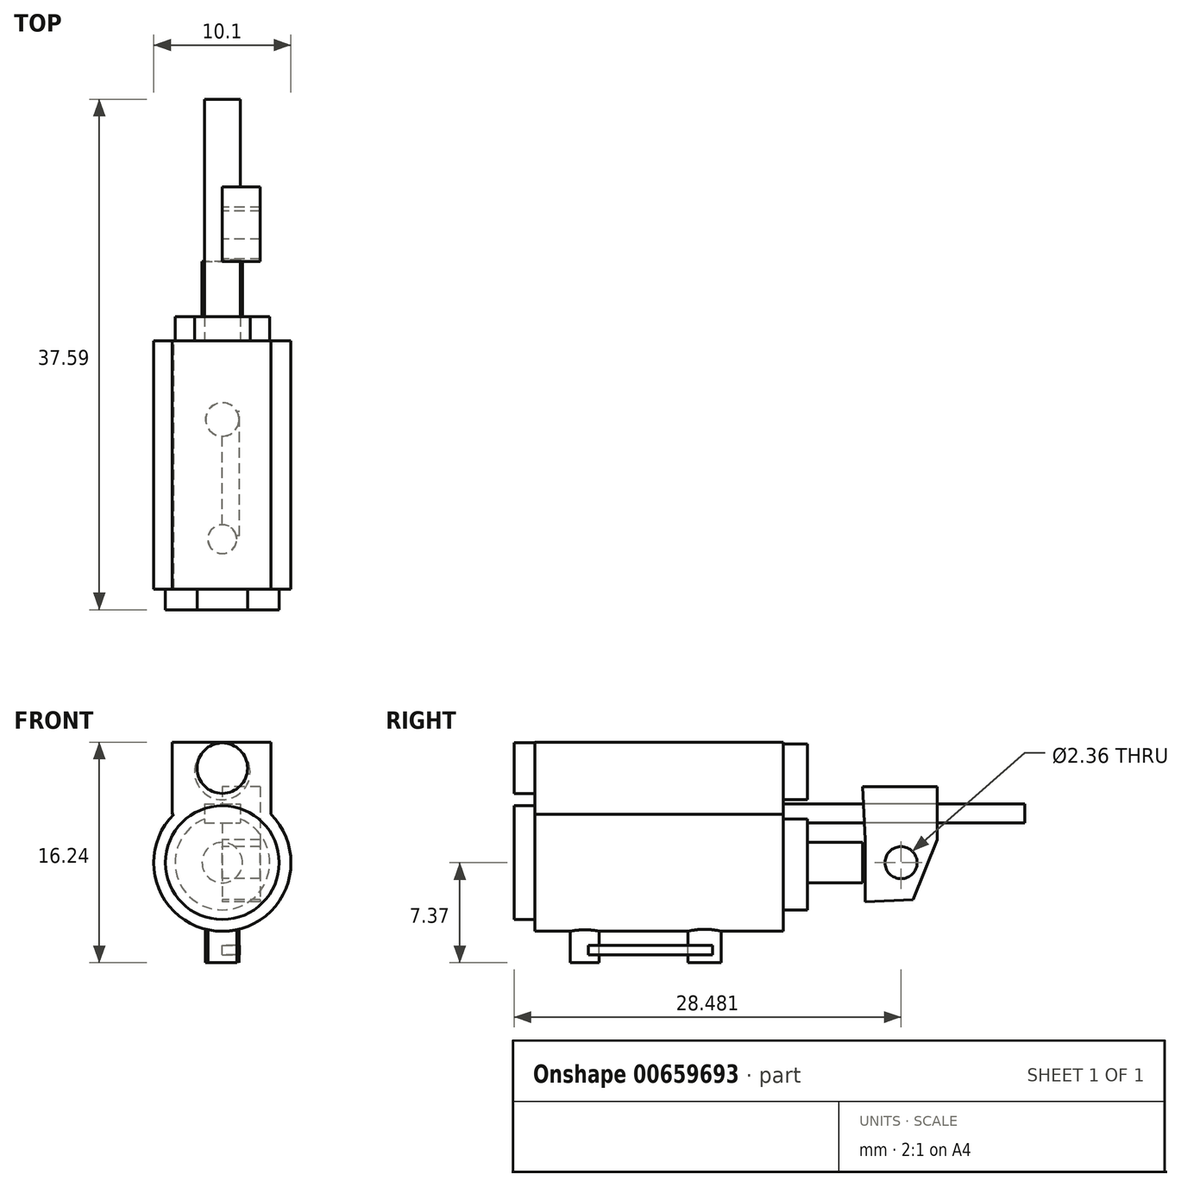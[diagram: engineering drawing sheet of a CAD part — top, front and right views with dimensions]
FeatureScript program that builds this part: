
annotation { "Feature Type Name" : "Feature", "Feature Type Description" : "" }
export const myFeature = defineFeature(function(context is Context, id is Id, definition is map)
    precondition{}
    {
        {
            var Q0;
            Q0=qCreatedBy(makeId("Front.planeOp"),FACE);
            var sketch = newSketch(context, id + "F0", { "sketchPlane" : qUnion([Q0])});
            skCircle(sketch, "E0", {"center": v(0, 0) * mm, "radius": 5.05 * mm});
            skLineSegment(sketch, "E1.bottom", {"start": v(-3.69, 8.87) * mm, "end": v(3.58, 8.87) * mm});
            skLineSegment(sketch, "E1.top", {"start": v(-3.69, 3.57) * mm, "end": v(3.58, 3.57) * mm});
            skLineSegment(sketch, "E1.left", {"start": v(-3.69, 8.87) * mm, "end": v(-3.69, 3.57) * mm});
            skLineSegment(sketch, "E1.right", {"start": v(3.58, 8.87) * mm, "end": v(3.58, 3.57) * mm});
            skSolve(sketch);
        }
        {
            var Q0;
            Q0 = qSketchRegion(id + "F0", true);
            extrude(context, id + "F1", {"entities" : qUnion([Q0]), "depth" : 18.29 * mm, "offsetDistance" : 25.4 * mm});
        }
        {
            var Q0;
            Q0=qCreatedBy(makeId("Front.planeOp"),FACE);
            var sketch = newSketch(context, id + "F2", { "sketchPlane" : qUnion([Q0])});
            skCircle(sketch, "E2", {"center": v(0, 0) * mm, "radius": 3.48 * mm});
            skCircle(sketch, "E3", {"center": v(0, 6.69) * mm, "radius": 2.05 * mm});
            skSolve(sketch);
        }
        {
            var Q0;
            Q0 = qSketchRegion(id + "F2", true);
            extrude(context, id + "F3", {"entities" : qUnion([Q0]), "operationType" : NewBodyOperationType.ADD, "oppositeDirection" : true, "depth" : 1.78 * mm, "offsetDistance" : 25.4 * mm});
        }
        {
            var Q0;
            Q0=qCreatedBy(makeId("Front.planeOp"),FACE);
            var sketch = newSketch(context, id + "F4", { "sketchPlane" : qUnion([Q0])});
            skCircle(sketch, "E4", {"center": v(0, 0) * mm, "radius": 4.19 * mm});
            skCircle(sketch, "E5", {"center": v(0, 6.96) * mm, "radius": 1.86 * mm});
            skSolve(sketch);
        }
        {
            var Q0;
            Q0 = qSketchRegion(id + "F4", true);
            extrude(context, id + "F5", {"entities" : qUnion([Q0]), "operationType" : NewBodyOperationType.ADD, "depth" : 19.8 * mm, "offsetDistance" : 25.4 * mm});
        }
        {
            var Q0;
            Q0=qCreatedBy(makeId("Top.planeOp"),FACE);
            var sketch = newSketch(context, id + "F6", { "sketchPlane" : qUnion([Q0])});
            skCircle(sketch, "E6", {"center": v(0, -14.6) * mm, "radius": 1.06 * mm});
            skCircle(sketch, "E7", {"center": v(0, -5.8) * mm, "radius": 1.24 * mm});
            skSolve(sketch);
        }
        {
            var Q0;
            Q0 = qSketchRegion(id + "F6", true);
            extrude(context, id + "F7", {"entities" : qUnion([Q0]), "operationType" : NewBodyOperationType.ADD, "oppositeDirection" : true, "depth" : 7.37 * mm, "offsetDistance" : 25.4 * mm});
        }
        {
            var Q0;
            Q0=qCreatedBy(makeId("Right.planeOp"),FACE);
            var sketch = newSketch(context, id + "F8", { "sketchPlane" : qUnion([Q0])});
            skLineSegment(sketch, "E8.bottom", {"start": v(-14.36, -6.78) * mm, "end": v(-5.2, -6.78) * mm});
            skLineSegment(sketch, "E8.top", {"start": v(-14.36, -6.08) * mm, "end": v(-5.2, -6.08) * mm});
            skLineSegment(sketch, "E8.left", {"start": v(-14.36, -6.78) * mm, "end": v(-14.36, -6.08) * mm});
            skLineSegment(sketch, "E8.right", {"start": v(-5.2, -6.78) * mm, "end": v(-5.2, -6.08) * mm});
            skSolve(sketch);
        }
        {
            var Q0;
            Q0 = qSketchRegion(id + "F8", true);
            extrude(context, id + "F9", {"entities" : qUnion([Q0]), "operationType" : NewBodyOperationType.ADD, "depth" : 1.27 * mm, "offsetDistance" : 25.4 * mm});
        }
        {
            var Q0;
            Q0=qCreatedBy(makeId("Front.planeOp"),FACE);
            var sketch = newSketch(context, id + "F10", { "sketchPlane" : qUnion([Q0])});
            skLineSegment(sketch, "E9.bottom", {"start": v(-1.32, 4.33) * mm, "end": v(1.32, 4.33) * mm});
            skLineSegment(sketch, "E9.top", {"start": v(-1.32, 2.91) * mm, "end": v(1.32, 2.91) * mm});
            skLineSegment(sketch, "E9.left", {"start": v(-1.32, 4.33) * mm, "end": v(-1.32, 2.91) * mm});
            skLineSegment(sketch, "E9.right", {"start": v(1.32, 4.33) * mm, "end": v(1.32, 2.91) * mm});
            skPoint(sketch, "E9.middle", {"position": v(0, 3.62) * mm});
            skSolve(sketch);
        }
        {
            var Q0;
            Q0 = qSketchRegion(id + "F10", true);
            extrude(context, id + "F11", {"entities" : qUnion([Q0]), "operationType" : NewBodyOperationType.ADD, "oppositeDirection" : true, "depth" : 17.78 * mm, "offsetDistance" : 25.4 * mm});
        }
        {
            var Q0;
            Q0=qCreatedBy(makeId("Right.planeOp"),FACE);
            var sketch = newSketch(context, id + "F12", { "sketchPlane" : qUnion([Q0])});
            skLineSegment(sketch, "E10", {"start": v(5.85, 5.6) * mm, "end": v(11.32, 5.6) * mm});
            skLineSegment(sketch, "E11", {"start": v(11.32, 5.6) * mm, "end": v(11.32, 1.7) * mm});
            skLineSegment(sketch, "E12", {"start": v(11.32, 1.7) * mm, "end": v(6.02, 1.7) * mm});
            skLineSegment(sketch, "E13", {"start": v(6.02, 1.7) * mm, "end": v(5.85, 5.6) * mm});
            skLineSegment(sketch, "E14", {"start": v(6.02, 1.7) * mm, "end": v(6.02, -2.89) * mm});
            skLineSegment(sketch, "E15", {"start": v(11.32, 1.7) * mm, "end": v(9.55, -2.71) * mm});
            skLineSegment(sketch, "E16", {"start": v(9.55, -2.71) * mm, "end": v(6.02, -2.89) * mm});
            skCircle(sketch, "E17", {"center": v(8.67, 0) * mm, "radius": 1.18 * mm});
            skPoint(sketch, "E17.centerSnap0", {"position": v(8.67, 1.7) * mm});
            skSolve(sketch);
        }
        {
            var Q0;
            Q0 = qSketchRegion(id + "F12", true);
            extrude(context, id + "F13", {"entities" : qUnion([Q0]), "operationType" : NewBodyOperationType.ADD, "depth" : 2.8 * mm, "offsetDistance" : 25.4 * mm});
        }
        {
            var Q0;
            Q0=qCreatedBy(makeId("Front.planeOp"),FACE);
            var sketch = newSketch(context, id + "F14", { "sketchPlane" : qUnion([Q0])});
            skCircle(sketch, "E18", {"center": v(0, 0) * mm, "radius": 1.49 * mm});
            skSolve(sketch);
        }
        {
            var Q0;
            Q0 = qSketchRegion(id + "F14", true);
            extrude(context, id + "F15", {"entities" : qUnion([Q0]), "operationType" : NewBodyOperationType.ADD, "oppositeDirection" : true, "depth" : 5.84 * mm, "offsetDistance" : 25.4 * mm});
        }
    });
